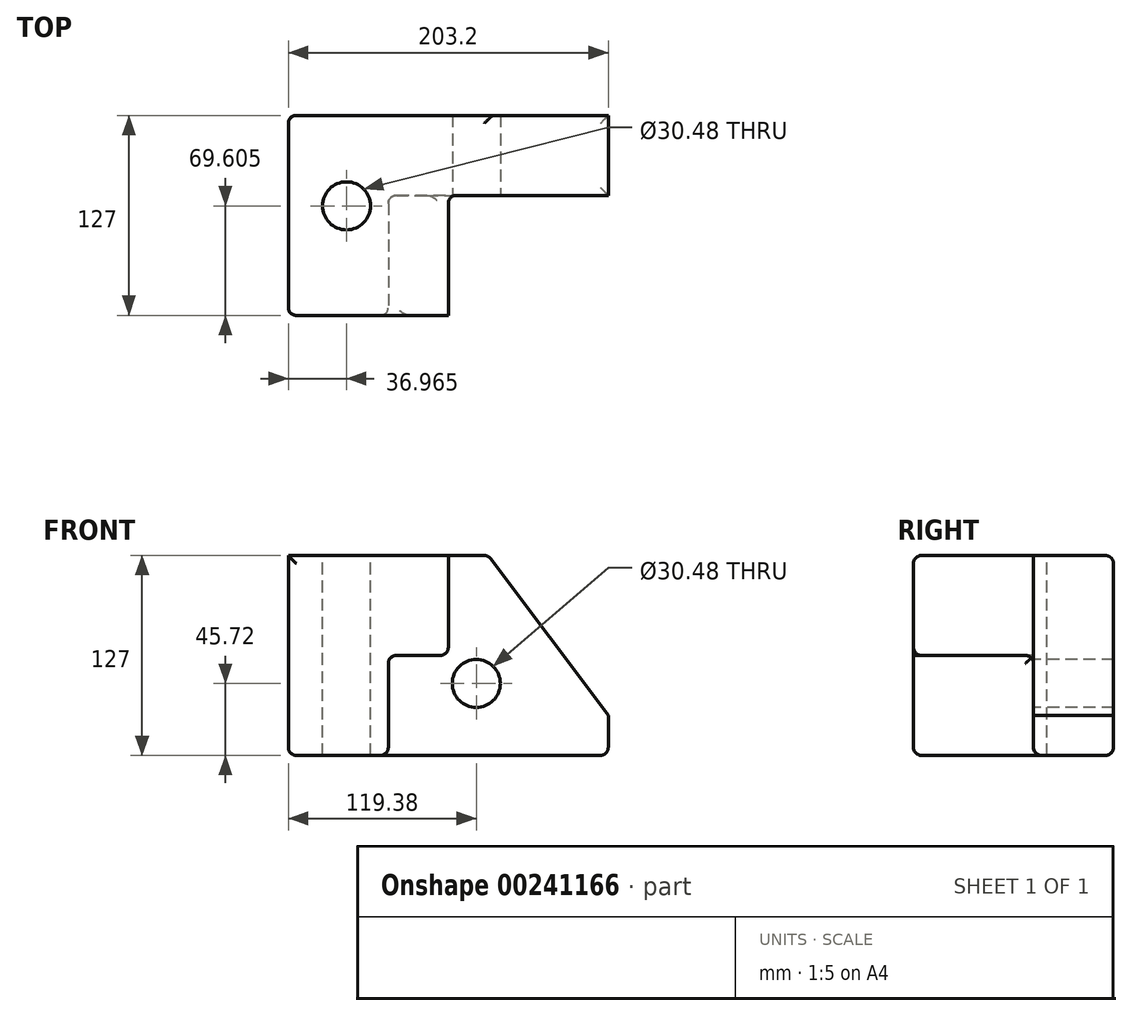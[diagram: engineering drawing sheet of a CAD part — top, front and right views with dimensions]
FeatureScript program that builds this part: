
annotation { "Feature Type Name" : "Feature", "Feature Type Description" : "" }
export const myFeature = defineFeature(function(context is Context, id is Id, definition is map)
    precondition{}
    {
        {
            var Q0;
            Q0=qCreatedBy(makeId("Front.planeOp"),FACE);
            var sketch = newSketch(context, id + "F0", { "sketchPlane" : qUnion([Q0])});
            skLineSegment(sketch, "E0.bottom", {"start": v(101.6, 63.5) * mm, "end": v(-101.6, 63.5) * mm});
            skLineSegment(sketch, "E0.top", {"start": v(101.6, -63.5) * mm, "end": v(-101.6, -63.5) * mm});
            skLineSegment(sketch, "E0.left", {"start": v(101.6, 63.5) * mm, "end": v(101.6, -63.5) * mm});
            skLineSegment(sketch, "E0.right", {"start": v(-101.6, 63.5) * mm, "end": v(-101.6, -63.5) * mm});
            skPoint(sketch, "E0.middle", {"position": v(0, 0) * mm});
            skSolve(sketch);
        }
        {
            var Q0;
            Q0 = qSketchRegion(id + "F0", true);
            extrude(context, id + "F1", {"entities" : qUnion([Q0]), "depth" : 127 * mm});
        }
        {
            var Q0;
            Q0=makeQuery(id+"F1.opExtrude","CAP_FACE",FACE,{"disambiguationData":[OSD([sQuery(id+"F0.wireOp",EDGE,"E0.bottom"),sQuery(id+"F0.wireOp",EDGE,"E0.top"),sQuery(id+"F0.wireOp",EDGE,"E0.left"),sQuery(id+"F0.wireOp",EDGE,"E0.right")])],"isStart":false});
            var sketch = newSketch(context, id + "F2", { "sketchPlane" : qUnion([Q0])});
            skLineSegment(sketch, "E1", {"start": v(-101.6, -63.5) * mm, "end": v(-38.1, -63.5) * mm});
            skLineSegment(sketch, "E2", {"start": v(-38.1, -63.5) * mm, "end": v(-38.1, 0) * mm});
            skLineSegment(sketch, "E3", {"start": v(-38.1, 0) * mm, "end": v(0, 0) * mm});
            skLineSegment(sketch, "E4", {"start": v(0, 0) * mm, "end": v(0, 63.5) * mm});
            skLineSegment(sketch, "E5", {"start": v(0, 63.5) * mm, "end": v(-101.6, 63.5) * mm});
            skLineSegment(sketch, "E6", {"start": v(-101.6, 63.5) * mm, "end": v(-101.6, -63.5) * mm});
            skSolve(sketch);
        }
        {
            var Q0;
            {var subQ3=sQuery(id+"F2.wireOp",EDGE,"E2");Q0=makeQuery(id+"F2.imprint","IMPRINT",FACE,{"disambiguationData":[TD([[makeQuery(id+"F2.imprint","IMPRINT",EDGE,{"derivedFrom":subQ3}),-1.0]])]});}
            extrude(context, id + "F3", {"entities" : qUnion([Q0]), "operationType" : NewBodyOperationType.REMOVE, "oppositeDirection" : true, "depth" : 76.2 * mm});
        }
        {
            var Q0;
            Q0=makeQuery(id+"F1.opExtrude","SWEPT_EDGE",EDGE,{"disambiguationData":[OSD([sQuery(id+"F0.wireOp",EDGE,"E0.bottom"),sQuery(id+"F0.wireOp",EDGE,"E0.left")])]});
            chamfer(context, id + "F4", {"entities" : qUnion([Q0]), "chamferType" : ChamferType.TWO_OFFSETS, "width1" : 76.2 * mm, "oppositeDirection" : false, "width2" : 101.6 * mm, "tangentPropagation" : true});
        }
        {
            var Q0;
            Q0=makeQuery(id+"F1.opExtrude","CAP_EDGE",EDGE,{"disambiguationData":[OSD([sQuery(id+"F0.wireOp",EDGE,"E0.bottom")])],"isStart":false});
            var Q1;
            Q1=makeQuery(id+"F3.boolean.opBoolean","COPY",EDGE,{"derivedFrom":makeQuery(id+"F3.opExtrude","CAP_EDGE",EDGE,{"disambiguationData":[OSD([sQuery(id+"F2.wireOp",EDGE,"E3")])],"isStart":true})});
            var Q2;
            Q2=makeQuery(id+"F3.boolean.opBoolean","COPY",EDGE,{"derivedFrom":makeQuery(id+"F3.opExtrude","SWEPT_EDGE",EDGE,{"disambiguationData":[OSD([sQuery(id+"F0.wireOp",EDGE,"E0.bottom"),sQuery(id+"F2.wireOp",EDGE,"E4"),sQuery(id+"F2.wireOp",EDGE,"E5")])]})});
            var Q3;
            Q3=makeQuery(id+"F3.boolean.opBoolean","COPY",EDGE,{"derivedFrom":makeQuery(id+"F3.opExtrude","SWEPT_EDGE",EDGE,{"disambiguationData":[OSD([sQuery(id+"F2.wireOp",EDGE,"E3"),sQuery(id+"F2.wireOp",EDGE,"E4")])]})});
            var Q4;
            Q4=makeQuery(id+"F3.boolean.opBoolean","COPY",EDGE,{"derivedFrom":makeQuery(id+"F3.opExtrude","CAP_EDGE",EDGE,{"disambiguationData":[OSD([sQuery(id+"F0.wireOp",EDGE,"E0.bottom")])],"isStart":false})});
            var Q5;
            {var subQ0=sQuery(id+"F0.wireOp",EDGE,"E0.bottom");Q5=makeQuery(id+"F4.opChamfer","BLEND_EDGE",EDGE,{"blendedFrom":[makeQuery(id+"F1.opExtrude","SWEPT_EDGE",EDGE,{"disambiguationData":[OSD([subQ0,sQuery(id+"F0.wireOp",EDGE,"E0.left")])]}),makeQuery(id+"F1.opExtrude","SWEPT_FACE",FACE,{"disambiguationData":[OSD([subQ0])]})],"blendedInto":[makeQuery(id+"F1.opExtrude","SWEPT_FACE",FACE,{"disambiguationData":[OSD([subQ0])]})]});}
            var Q6;
            Q6=makeQuery(id+"F1.opExtrude","CAP_EDGE",EDGE,{"disambiguationData":[OSD([sQuery(id+"F0.wireOp",EDGE,"E0.bottom")])],"isStart":true});
            var Q7;
            Q7=makeQuery(id+"F3.boolean.opBoolean","COPY",EDGE,{"derivedFrom":makeQuery(id+"F3.opExtrude","SWEPT_EDGE",EDGE,{"disambiguationData":[OSD([sQuery(id+"F0.wireOp",EDGE,"E0.top"),sQuery(id+"F2.wireOp",EDGE,"E1"),sQuery(id+"F2.wireOp",EDGE,"E2")])]})});
            var Q8;
            Q8=makeQuery(id+"F1.opExtrude","CAP_EDGE",EDGE,{"disambiguationData":[OSD([sQuery(id+"F0.wireOp",EDGE,"E0.top")])],"isStart":false});
            var Q9;
            Q9=makeQuery(id+"F3.boolean.opBoolean","COPY",EDGE,{"derivedFrom":makeQuery(id+"F3.opExtrude","CAP_EDGE",EDGE,{"disambiguationData":[OSD([sQuery(id+"F2.wireOp",EDGE,"E2")])],"isStart":true})});
            var Q10;
            Q10=makeQuery(id+"F1.opExtrude","CAP_EDGE",EDGE,{"disambiguationData":[OSD([sQuery(id+"F0.wireOp",EDGE,"E0.right")])],"isStart":false});
            var Q11;
            Q11=makeQuery(id+"F3.boolean.opBoolean","COPY",EDGE,{"derivedFrom":makeQuery(id+"F3.opExtrude","CAP_EDGE",EDGE,{"disambiguationData":[OSD([sQuery(id+"F0.wireOp",EDGE,"E0.top")])],"isStart":false})});
            var Q12;
            Q12=makeQuery(id+"F1.opExtrude","SWEPT_EDGE",EDGE,{"disambiguationData":[OSD([sQuery(id+"F0.wireOp",EDGE,"E0.top"),sQuery(id+"F0.wireOp",EDGE,"E0.left")])]});
            var Q13;
            Q13=makeQuery(id+"F3.boolean.opBoolean","COPY",EDGE,{"derivedFrom":makeQuery(id+"F3.opExtrude","CAP_EDGE",EDGE,{"disambiguationData":[OSD([sQuery(id+"F2.wireOp",EDGE,"E2")])],"isStart":false})});
            var Q14;
            Q14=makeQuery(id+"F3.boolean.opBoolean","COPY",EDGE,{"derivedFrom":makeQuery(id+"F3.opExtrude","CAP_EDGE",EDGE,{"disambiguationData":[OSD([sQuery(id+"F2.wireOp",EDGE,"E4")])],"isStart":false})});
            var Q15;
            Q15=makeQuery(id+"F3.boolean.opBoolean","COPY",FACE,{"derivedFrom":makeQuery(id+"F3.opExtrude","SWEPT_FACE",FACE,{"disambiguationData":[OSD([sQuery(id+"F2.wireOp",EDGE,"E2")])]})});
            var Q16;
            Q16=makeQuery(id+"F1.opExtrude","SWEPT_FACE",FACE,{"disambiguationData":[OSD([sQuery(id+"F0.wireOp",EDGE,"E0.top")])]});
            var Q17;
            Q17=makeQuery(id+"F1.opExtrude","CAP_EDGE",EDGE,{"disambiguationData":[OSD([sQuery(id+"F0.wireOp",EDGE,"E0.right")])],"isStart":true});
            fillet(context, id + "F5", {"entities" : qUnion([Q0, Q1, Q2, Q3, Q4, Q5, Q6, Q7, Q8, Q9, Q10, Q11, Q12, Q13, Q14, Q15, Q16, Q17]), "radius" : 5.08 * mm, "tangentPropagation" : true, "allowEdgeOverflow" : false});
        }
        {
            var Q0;
            Q0=makeQuery(id+"F3.boolean.opBoolean","COPY",FACE,{"derivedFrom":makeQuery(id+"F3.opExtrude","CAP_FACE",FACE,{"disambiguationData":[OSD([sQuery(id+"F0.wireOp",EDGE,"E0.bottom"),sQuery(id+"F0.wireOp",EDGE,"E0.top"),sQuery(id+"F0.wireOp",EDGE,"E0.left"),sQuery(id+"F2.wireOp",EDGE,"E2"),sQuery(id+"F2.wireOp",EDGE,"E3"),sQuery(id+"F2.wireOp",EDGE,"E4")])],"isStart":false})});
            var sketch = newSketch(context, id + "F6", { "sketchPlane" : qUnion([Q0])});
            skCircle(sketch, "E7", {"center": v(17.78, -17.78) * mm, "radius": 15.24 * mm});
            skSolve(sketch);
        }
        {
            var Q0;
            Q0=makeQuery(id+"F6.imprint","IMPRINT",FACE,{"disambiguationData":[TD([[makeQuery(id+"F6.imprint","IMPRINT",EDGE,{"derivedFrom":sQuery(id+"F6.wireOp",EDGE,"E7")}),1.0]])]});
            var Q1;
            Q1=makeQuery(id+"F1.opExtrude","CAP_FACE",FACE,{"disambiguationData":[OSD([sQuery(id+"F0.wireOp",EDGE,"E0.bottom"),sQuery(id+"F0.wireOp",EDGE,"E0.top"),sQuery(id+"F0.wireOp",EDGE,"E0.left"),sQuery(id+"F0.wireOp",EDGE,"E0.right")])],"isStart":true});
            extrude(context, id + "F7", {"entities" : qUnion([Q0]), "operationType" : NewBodyOperationType.REMOVE, "endBound" : BoundingType.UP_TO_SURFACE, "oppositeDirection" : true, "endBoundEntityFace" : qUnion([Q1]), "depth" : 25.4 * mm});
        }
        {
            var Q0;
            Q0=makeQuery(id+"F1.opExtrude","SWEPT_FACE",FACE,{"disambiguationData":[OSD([sQuery(id+"F0.wireOp",EDGE,"E0.bottom")])]});
            var sketch = newSketch(context, id + "F8", { "sketchPlane" : qUnion([Q0])});
            skCircle(sketch, "E8", {"center": v(-64.64, -57.4) * mm, "radius": 15.24 * mm});
            skSolve(sketch);
        }
        {
            var Q0;
            Q0=makeQuery(id+"F8.imprint","IMPRINT",FACE,{"disambiguationData":[TD([[makeQuery(id+"F8.imprint","IMPRINT",EDGE,{"derivedFrom":sQuery(id+"F8.wireOp",EDGE,"E8")}),1.0]])]});
            var Q1;
            Q1=makeQuery(id+"F1.opExtrude","SWEPT_FACE",FACE,{"disambiguationData":[OSD([sQuery(id+"F0.wireOp",EDGE,"E0.top")])]});
            extrude(context, id + "F9", {"entities" : qUnion([Q0]), "operationType" : NewBodyOperationType.REMOVE, "endBound" : BoundingType.UP_TO_SURFACE, "oppositeDirection" : true, "endBoundEntityFace" : qUnion([Q1]), "depth" : 25.4 * mm});
        }
    });
